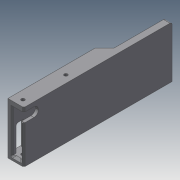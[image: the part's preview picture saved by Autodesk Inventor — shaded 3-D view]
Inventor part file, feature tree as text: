
AUTODESK INVENTOR PART (.ipt)
format: ipt  version: 2020.4 (Build 244396000, 396)  size: 269,312 bytes
history: native  units: in
note: dims shown in document units (in); Inventor stores cm internally (conversion verified against a paired STEP export)
features: chamfer x6, fillet x6, extrude x5, sketch x5, hole x1, mirror x1
ambient origin geometry x8: Origin, YZ Plane, XZ Plane, XY Plane, X Axis, Y Axis, Z Axis, Center Point
bodies: Solid1 (feature_tree)
feature tree (24):
  extrude  "Extrusion1"  Depth=0.25in
  hole  "Hole1"  [1 undecoded]
  extrude  "Extrusion2"  Depth=1.25in
  chamfer  "Chamfer1"  Distance=0.39in
  chamfer  "Chamfer4"  Distance=0.13in
  extrude  "Extrusion4"  Depth=0.425in
  extrude  "Extrusion5"  Depth=0.125in TaperAngle=45.0deg
  fillet  "Fillet2"  Radius=0.5in
  fillet  "Fillet3"  Radius=0.25in
  chamfer  "Chamfer5"  Angle=45.0deg  [1 undecoded]
  chamfer  "Chamfer6"  [1 undecoded]
  fillet  "Fillet4"  Radius=0.5in
  chamfer  "Chamfer7"  Distance=1.5in
  fillet  "Fillet5"  Radius=1.0in
  chamfer  "Chamfer8"  Distance=0.125in
  extrude  "Extrusion6"  Depth=0.125in
  fillet  "Fillet6"  Radius=0.25in
  fillet  "Fillet7"  Radius=0.125in
  mirror  "Mirror1"
  sketch  "Sketch2"  dims[d1=0.25in d2=0.25in]
  sketch  "Sketch3"  dims[d4=0.5in d5=1.625in d6=0.0in]
  sketch  "Sketch5"  dims[d7=1.25in d8=1.25in]
  sketch  "Sketch6"  dims[d9=0.201in d10=0.224in d11=0.375in d12=0.19in d13=0.5635in d14=1.0in d15=0.8108in]
  sketch  "Sketch7"  dims[d16=3.0in d17=0.39in d18=0.13in d19=0.0in d20=0.425in d23=0.125in d24=0.125in d25=45.0deg d33=0.5in d39=0.25in d40=7.0in d41=0.0in d42=0.075in d43=0.125in d44=45.0deg d45=45.0deg d47=0.0in d48=0.0in d49=0.5in d50=1.5in d51=1.0in d52=0.0in d53=0.125in d54=0.125in d55=0.25in d56=0.125in d57=45.0deg d58=0.075in d59=0.125in d60=45.0deg d61=0.125in d62=0.2in d64=5.625in d65=0.125in d66=0.125in d67=45.0deg d68=0.125in d69=0.225in d71=0.05in d72=0.125in d73=45.0deg d74=0.25in d75=0.54in d76=0.85in d77=1.0in d78=0.0in d79=0.26in d80=0.05in]
note: 3 required parameter values undecoded (feature->parameter linkage not recoverable at this tier; creation-order binding heuristic only, values carry confidence <= 0.55)
